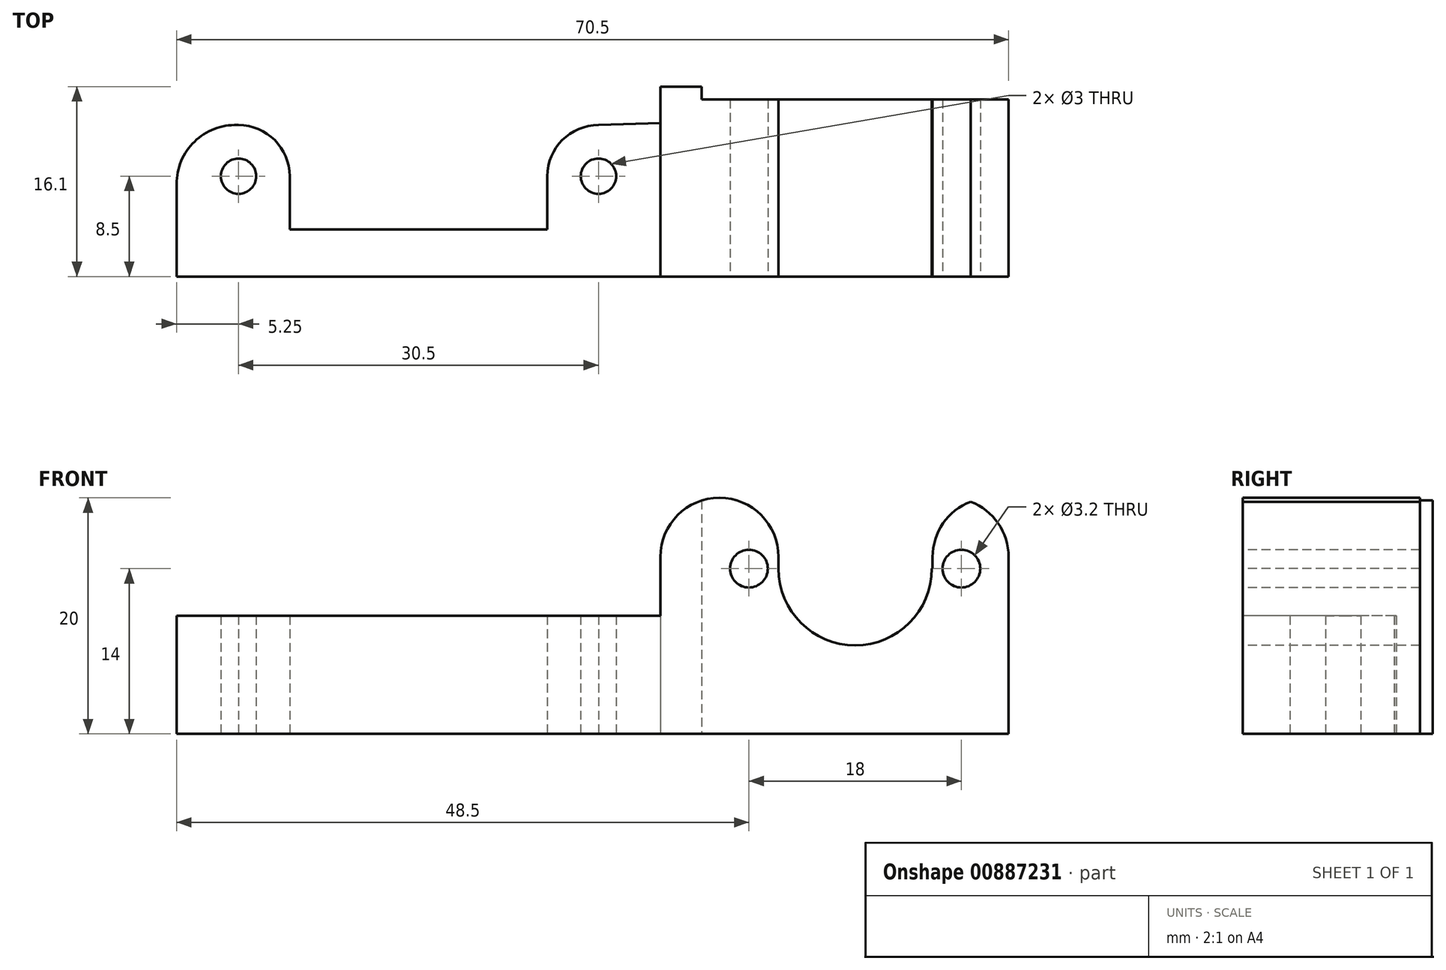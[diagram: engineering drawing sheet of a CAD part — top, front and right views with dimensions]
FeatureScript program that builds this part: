
annotation { "Feature Type Name" : "Feature", "Feature Type Description" : "" }
export const myFeature = defineFeature(function(context is Context, id is Id, definition is map)
    precondition{}
    {
        {
            var Q0;
            Q0=qCreatedBy(makeId("Top.planeOp"),FACE);
            var sketch = newSketch(context, id + "F0", { "sketchPlane" : qUnion([Q0])});
            skLineSegment(sketch, "E0.bottom", {"start": v(20.5, 4.5) * mm, "end": v(-20.5, 4.5) * mm});
            skLineSegment(sketch, "E0.top", {"start": v(20.5, -4.5) * mm, "end": v(-20.5, -4.5) * mm});
            skLineSegment(sketch, "E0.left", {"start": v(20.5, 4.5) * mm, "end": v(20.5, -4.5) * mm});
            skLineSegment(sketch, "E0.right", {"start": v(-20.5, 4.5) * mm, "end": v(-20.5, -4.5) * mm});
            skPoint(sketch, "E0.middle", {"position": v(0, 0) * mm});
            skCircle(sketch, "E1", {"center": v(-15.25, 0) * mm, "radius": 1.5 * mm});
            skCircle(sketch, "E2", {"center": v(15.25, 0) * mm, "radius": 1.5 * mm});
            skArc(sketch, "E3", {"start": v(-10.91, 0) * mm, "mid": v(-12.18, 3.07) * mm, "end": v(-15.25, 4.34) * mm});
            skArc(sketch, "E4", {"start": v(10.91, 0) * mm, "mid": v(12.18, 3.07) * mm, "end": v(15.25, 4.34) * mm});
            skLineSegment(sketch, "E5", {"start": v(-10.91, 0) * mm, "end": v(-10.91, -4.5) * mm});
            skLineSegment(sketch, "E6", {"start": v(10.91, 0) * mm, "end": v(10.91, -4.5) * mm});
            skLineSegment(sketch, "E7.top", {"start": v(20.5, -8.5) * mm, "end": v(-20.5, -8.5) * mm});
            skLineSegment(sketch, "E7.left", {"start": v(20.5, -4.5) * mm, "end": v(20.5, -8.5) * mm});
            skLineSegment(sketch, "E7.right", {"start": v(-20.5, -4.5) * mm, "end": v(-20.5, -8.5) * mm});
            skLineSegment(sketch, "E8", {"start": v(-15.25, 4.34) * mm, "end": v(-20.5, 4.5) * mm});
            skLineSegment(sketch, "E9", {"start": v(15.25, 4.34) * mm, "end": v(20.5, 4.5) * mm});
            skLineSegment(sketch, "E10.right", {"start": v(24, 0) * mm, "end": v(24, 7.6) * mm});
            skLineSegment(sketch, "E11.bottom", {"start": v(24, 7.6) * mm, "end": v(20.5, 7.6) * mm});
            skLineSegment(sketch, "E11.top", {"start": v(24, -8.5) * mm, "end": v(20.5, -8.5) * mm});
            skLineSegment(sketch, "E11.left", {"start": v(24, 7.6) * mm, "end": v(24, -8.5) * mm});
            skLineSegment(sketch, "E11.right", {"start": v(20.5, 7.6) * mm, "end": v(20.5, -8.5) * mm});
            skSolve(sketch);
        }
        {
            var Q0;
            {var subQ1=sQuery(id+"F0.wireOp",EDGE,"E0.right");Q0=makeQuery(id+"F0.imprint","IMPRINT",FACE,{"disambiguationData":[TD([[makeQuery(id+"F0.imprint","IMPRINT",EDGE,{"derivedFrom":subQ1}),1.0]])]});}
            var Q1;
            Q1=makeQuery(id+"F0.imprint","IMPRINT",FACE,{"disambiguationData":[TD([[makeQuery(id+"F0.imprint","IMPRINT",EDGE,{"derivedFrom":sQuery(id+"F0.wireOp",EDGE,"E7.top")}),-1.0]])]});
            var Q2;
            {var subQ1=sQuery(id+"F0.wireOp",EDGE,"E0.left");Q2=makeQuery(id+"F0.imprint","IMPRINT",FACE,{"disambiguationData":[TD([[makeQuery(id+"F0.imprint","IMPRINT",EDGE,{"derivedFrom":subQ1}),-1.0]])]});}
            var Q3;
            Q3=makeQuery(id+"F0.imprint","IMPRINT",FACE,{"disambiguationData":[TD([[makeQuery(id+"F0.imprint","IMPRINT",EDGE,{"derivedFrom":sQuery(id+"F0.wireOp",EDGE,"E2")}),-1.0]])]});
            extrude(context, id + "F1", {"entities" : qUnion([Q0, Q1, Q2, Q3]), "depth" : 10 * mm, "offsetDistance" : 25 * mm});
        }
        {
            var Q0;
            {var subQ2=sQuery(id+"F0.wireOp",EDGE,"E11.bottom");Q0=makeQuery(id+"F0.imprint","IMPRINT",FACE,{"disambiguationData":[TD([[makeQuery(id+"F0.imprint","IMPRINT",EDGE,{"derivedFrom":subQ2}),1.0]])]});}
            extrude(context, id + "F2", {"entities" : qUnion([Q0]), "depth" : 20 * mm, "offsetDistance" : 25 * mm});
        }
        {
            var Q0;
            Q0=makeQuery(id+"F1.opExtrude","SWEPT_BODY",BODY,{"disambiguationData":[OSD([sQuery(id+"F0.wireOp",EDGE,"E0.right"),sQuery(id+"F0.wireOp",EDGE,"E1"),sQuery(id+"F0.wireOp",EDGE,"E2"),sQuery(id+"F0.wireOp",EDGE,"E3"),sQuery(id+"F0.wireOp",EDGE,"E4"),sQuery(id+"F0.wireOp",EDGE,"E5"),sQuery(id+"F0.wireOp",EDGE,"E6"),sQuery(id+"F0.wireOp",EDGE,"E0.top"),sQuery(id+"F0.wireOp",EDGE,"E7.top"),sQuery(id+"F0.wireOp",EDGE,"E7.right"),sQuery(id+"F0.wireOp",EDGE,"E8"),sQuery(id+"F0.wireOp",EDGE,"E9"),sQuery(id+"F0.wireOp",EDGE,"E11.right")])]});
            var Q1;
            Q1=makeQuery(id+"F2.opExtrude","SWEPT_BODY",BODY,{"disambiguationData":[OSD([sQuery(id+"F0.wireOp",EDGE,"E11.bottom"),sQuery(id+"F0.wireOp",EDGE,"E11.top"),sQuery(id+"F0.wireOp",EDGE,"E11.left"),sQuery(id+"F0.wireOp",EDGE,"E11.right")])]});
            booleanBodies(context, id + "F3", {"operationType" : BooleanOperationType.UNION, "tools" : qUnion([Q0, Q1])});
        }
        {
            var Q0;
            Q0=makeQuery(id+"F3.opBoolean","MERGE",FACE,{"derivedFrom":[makeQuery(id+"F1.opExtrude","SWEPT_FACE",FACE,{"disambiguationData":[OSD([sQuery(id+"F0.wireOp",EDGE,"E7.top")])]}),makeQuery(id+"F2.opExtrude","SWEPT_FACE",FACE,{"disambiguationData":[OSD([sQuery(id+"F0.wireOp",EDGE,"E11.top")])]})]});
            var sketch = newSketch(context, id + "F4", { "sketchPlane" : qUnion([Q0])});
            skLineSegment(sketch, "E12.bottom", {"start": v(24, 0) * mm, "end": v(50, 0) * mm});
            skLineSegment(sketch, "E12.top", {"start": v(24, 20) * mm, "end": v(50, 20) * mm});
            skLineSegment(sketch, "E12.left", {"start": v(24, 0) * mm, "end": v(24, 20) * mm});
            skLineSegment(sketch, "E12.right", {"start": v(50, 0) * mm, "end": v(50, 20) * mm});
            skLineSegment(sketch, "E13.left", {"start": v(24, 0) * mm, "end": v(24, 14) * mm});
            skLineSegment(sketch, "E13.right", {"start": v(50, 0) * mm, "end": v(50, 14) * mm});
            skCircle(sketch, "E14", {"center": v(37, 14) * mm, "radius": 6.5 * mm});
            skCircle(sketch, "E15", {"center": v(28, 14) * mm, "radius": 1.6 * mm});
            skCircle(sketch, "E16", {"center": v(46, 14) * mm, "radius": 1.6 * mm});
            skLineSegment(sketch, "E17.bottom", {"start": v(30.5, 14) * mm, "end": v(43.56, 14) * mm});
            skLineSegment(sketch, "E17.top", {"start": v(30.5, 20) * mm, "end": v(43.56, 20) * mm});
            skLineSegment(sketch, "E17.left", {"start": v(30.5, 14) * mm, "end": v(30.5, 20) * mm});
            skLineSegment(sketch, "E17.right", {"start": v(43.56, 14) * mm, "end": v(43.56, 20) * mm});
            skSolve(sketch);
        }
        {
            var Q0;
            {var subQ4=sQuery(id+"F4.wireOp",EDGE,"E12.left");Q0=makeQuery(id+"F4.imprint","IMPRINT",FACE,{"disambiguationData":[TD([[makeQuery(id+"F4.imprint","IMPRINT",EDGE,{"derivedFrom":subQ4}),1.0]])]});}
            extrude(context, id + "F5", {"entities" : qUnion([Q0]), "operationType" : NewBodyOperationType.ADD, "oppositeDirection" : true, "depth" : 15 * mm, "offsetDistance" : 25 * mm});
        }
        {
            var Q0;
            Q0=makeQuery(id+"F5.opExtrude","SWEPT_EDGE",EDGE,{"disambiguationData":[OSD([sQuery(id+"F4.wireOp",EDGE,"E12.top"),sQuery(id+"F4.wireOp",EDGE,"E17.top"),sQuery(id+"F4.wireOp",EDGE,"E17.right")])]});
            var Q1;
            Q1=makeQuery(id+"F5.opExtrude","SWEPT_EDGE",EDGE,{"disambiguationData":[OSD([sQuery(id+"F4.wireOp",EDGE,"E12.top"),sQuery(id+"F4.wireOp",EDGE,"E12.right")])]});
            var Q2;
            Q2=makeQuery(id+"F5.opExtrude","SWEPT_EDGE",EDGE,{"disambiguationData":[OSD([sQuery(id+"F4.wireOp",EDGE,"E12.top"),sQuery(id+"F4.wireOp",EDGE,"E17.top"),sQuery(id+"F4.wireOp",EDGE,"E17.left")])]});
            var Q3;
            Q3=makeQuery(id+"F2.opExtrude","CAP_EDGE",EDGE,{"disambiguationData":[OSD([sQuery(id+"F0.wireOp",EDGE,"E11.right")])],"isStart":false});
            var Q4;
            Q4=makeQuery(id+"F1.opExtrude","SWEPT_EDGE",EDGE,{"disambiguationData":[OSD([sQuery(id+"F0.wireOp",EDGE,"E0.bottom"),sQuery(id+"F0.wireOp",EDGE,"E0.right"),sQuery(id+"F0.wireOp",EDGE,"E8")])]});
            fillet(context, id + "F6", {"entities" : qUnion([Q0, Q1, Q2, Q3, Q4]), "radius" : 5 * mm, "tangentPropagation" : true, "allowEdgeOverflow" : false});
        }
    });
